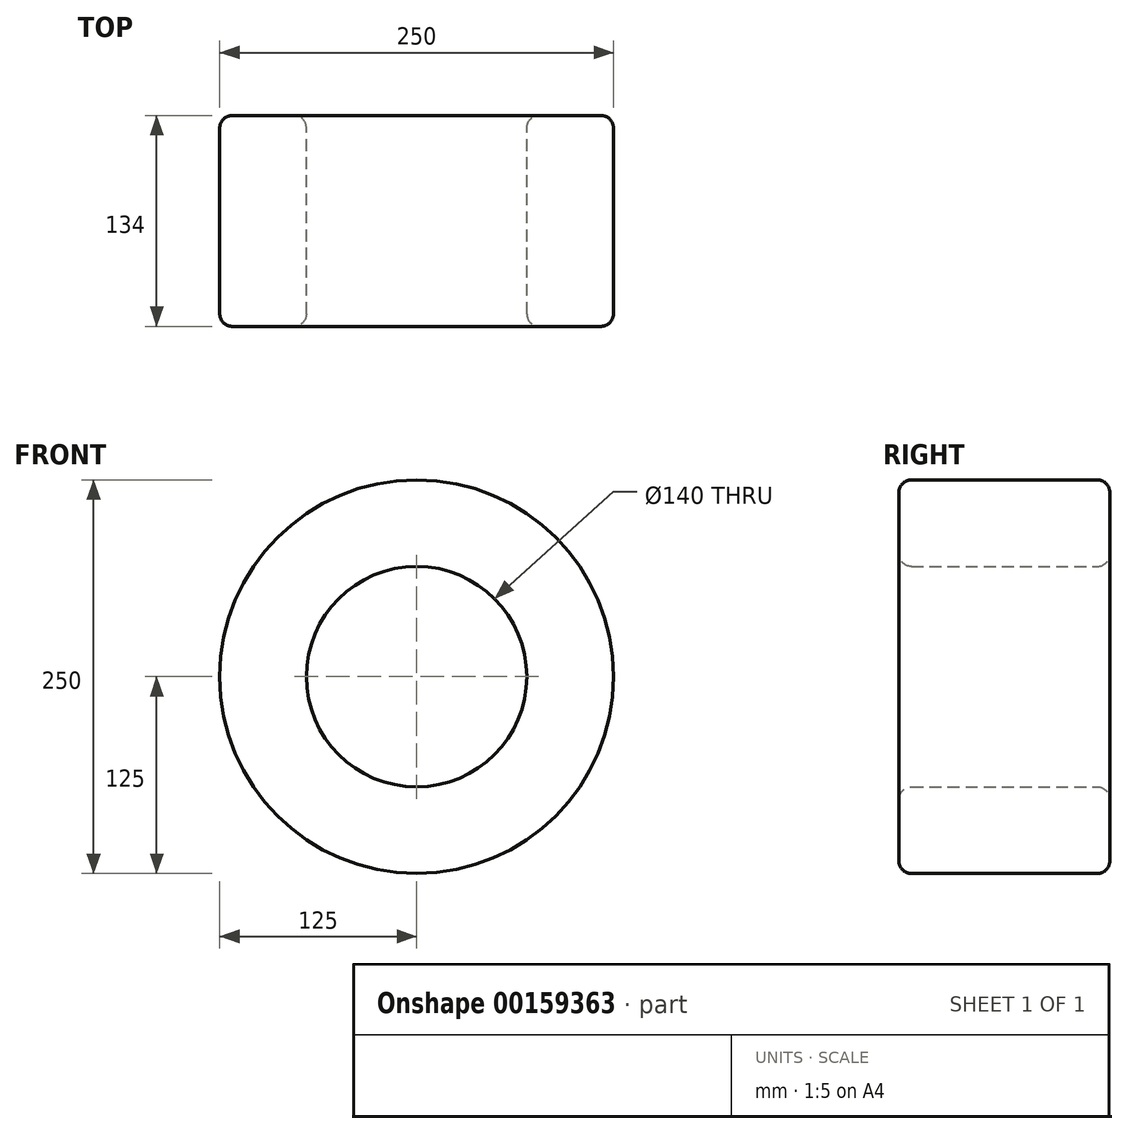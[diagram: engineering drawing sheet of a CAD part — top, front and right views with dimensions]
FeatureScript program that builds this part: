
annotation { "Feature Type Name" : "Feature", "Feature Type Description" : "" }
export const myFeature = defineFeature(function(context is Context, id is Id, definition is map)
    precondition{}
    {
        {
            var Q0;
            Q0=qCreatedBy(makeId("Front.planeOp"),FACE);
            var sketch = newSketch(context, id + "F0", { "sketchPlane" : qUnion([Q0])});
            skCircle(sketch, "E0", {"center": v(0, 0) * mm, "radius": 125 * mm});
            skCircle(sketch, "E1", {"center": v(0, 0) * mm, "radius": 70 * mm});
            skSolve(sketch);
        }
        {
            var Q0;
            Q0=makeQuery(id+"F0.imprint","IMPRINT",FACE,{"disambiguationData":[TD([[makeQuery(id+"F0.imprint","IMPRINT",EDGE,{"derivedFrom":sQuery(id+"F0.wireOp",EDGE,"E0")}),1.0]])]});
            extrude(context, id + "F1", {"entities" : qUnion([Q0]), "depth" : 134 * mm, "symmetric" : true});
        }
        {
            var Q0;
            Q0=makeQuery(id+"F1.opExtrude","CAP_EDGE",EDGE,{"disambiguationData":[OSD([sQuery(id+"F0.wireOp",EDGE,"E0")])],"isStart":false});
            var Q1;
            Q1=makeQuery(id+"F1.opExtrude","CAP_EDGE",EDGE,{"disambiguationData":[OSD([sQuery(id+"F0.wireOp",EDGE,"E0")])],"isStart":true});
            var Q2;
            Q2=makeQuery(id+"F1.opExtrude","CAP_EDGE",EDGE,{"disambiguationData":[OSD([sQuery(id+"F0.wireOp",EDGE,"E1")])],"isStart":true});
            var Q3;
            Q3=makeQuery(id+"F1.opExtrude","CAP_EDGE",EDGE,{"disambiguationData":[OSD([sQuery(id+"F0.wireOp",EDGE,"E1")])],"isStart":false});
            fillet(context, id + "F2", {"entities" : qUnion([Q0, Q1, Q2, Q3]), "radius" : 8 * mm, "tangentPropagation" : true, "allowEdgeOverflow" : false});
        }
    });
